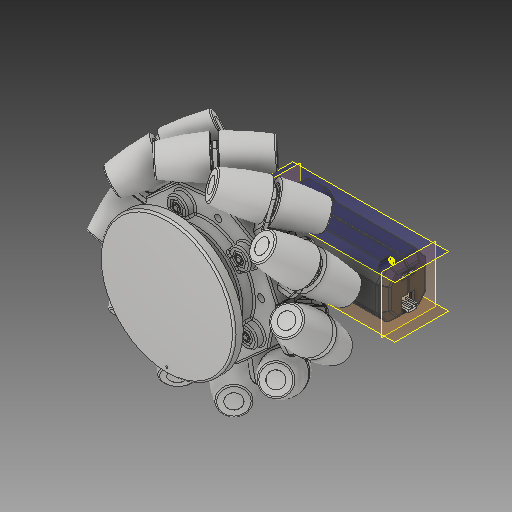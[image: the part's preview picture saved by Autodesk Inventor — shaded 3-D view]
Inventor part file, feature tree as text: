
AUTODESK INVENTOR PART (.ipt)
format: ipt  version: 2019 (Build 230136000, 136)  size: 17,352,704 bytes
history: native  units: in
note: dims shown in document units (in); Inventor stores cm internally (conversion verified against a paired STEP export)
features: other x108, plane x4
ambient origin geometry x8: Origin, YZ Plane, XZ Plane, XY Plane, X Axis, Y Axis, Z Axis, Center Point
bodies: Solid1 (feature_tree)
feature tree (112):
  other  "Wheel Sub-Assembly.iam"
  other  "wheel hubcap.ipt:1"
  other  "6inchMecanumLeft217-2799.20121203.iam:1::217-2799-001 Rev1.ipt:1"
  other  "6inchMecanumLeft217-2799.20121203.iam:1::217-2799-001 Rev1.ipt:2"
  other  "6inchMecanumLeft217-2799.20121203.iam:1::217-2799-002 Rev1.ipt:1"
  other  "6inchMecanumLeft217-2799.20121203.iam:1::217-2586-003 Rev2.ipt:1"
  other  "6inchMecanumLeft217-2799.20121203.iam:1::217-2586-003 Rev2.ipt:2"
  other  "6inchMecanumLeft217-2799.20121203.iam:1::217-2586-004 Rev1.ipt:1"
  other  "6inchMecanumLeft217-2799.20121203.iam:1::217-2586-004 Rev1.ipt:2"
  other  "6inchMecanumLeft217-2799.20121203.iam:1::217-2586-007 Rev1.ipt:1"
  other  "6inchMecanumLeft217-2799.20121203.iam:1::217-2586-008 Rev1.ipt:1"
  other  "6inchMecanumLeft217-2799.20121203.iam:1::NUT-832-NYLOCK.ipt:1"
  other  "6inchMecanumLeft217-2799.20121203.iam:1::SCREW-832-1250.ipt:1"
  other  "6inchMecanumLeft217-2799.20121203.iam:1::217-2586-007 Rev1.ipt:2"
  other  "6inchMecanumLeft217-2799.20121203.iam:1::217-2586-007 Rev1.ipt:3"
  other  "6inchMecanumLeft217-2799.20121203.iam:1::217-2586-007 Rev1.ipt:4"
  other  "6inchMecanumLeft217-2799.20121203.iam:1::217-2586-007 Rev1.ipt:5"
  other  "6inchMecanumLeft217-2799.20121203.iam:1::217-2586-007 Rev1.ipt:6"
  other  "6inchMecanumLeft217-2799.20121203.iam:1::217-2586-007 Rev1.ipt:7"
  other  "6inchMecanumLeft217-2799.20121203.iam:1::217-2586-007 Rev1.ipt:8"
  other  "6inchMecanumLeft217-2799.20121203.iam:1::217-2586-007 Rev1.ipt:9"
  other  "6inchMecanumLeft217-2799.20121203.iam:1::217-2586-007 Rev1.ipt:10"
  other  "6inchMecanumLeft217-2799.20121203.iam:1::217-2586-004 Rev1.ipt:3"
  other  "6inchMecanumLeft217-2799.20121203.iam:1::217-2586-004 Rev1.ipt:4"
  other  "6inchMecanumLeft217-2799.20121203.iam:1::217-2586-004 Rev1.ipt:5"
  other  "6inchMecanumLeft217-2799.20121203.iam:1::217-2586-004 Rev1.ipt:6"
  other  "6inchMecanumLeft217-2799.20121203.iam:1::217-2586-004 Rev1.ipt:7"
  other  "6inchMecanumLeft217-2799.20121203.iam:1::217-2586-004 Rev1.ipt:8"
  other  "6inchMecanumLeft217-2799.20121203.iam:1::217-2586-004 Rev1.ipt:9"
  other  "6inchMecanumLeft217-2799.20121203.iam:1::217-2586-004 Rev1.ipt:10"
  other  "6inchMecanumLeft217-2799.20121203.iam:1::217-2586-004 Rev1.ipt:11"
  other  "6inchMecanumLeft217-2799.20121203.iam:1::217-2586-004 Rev1.ipt:12"
  other  "6inchMecanumLeft217-2799.20121203.iam:1::217-2586-004 Rev1.ipt:13"
  other  "6inchMecanumLeft217-2799.20121203.iam:1::217-2586-004 Rev1.ipt:14"
  other  "6inchMecanumLeft217-2799.20121203.iam:1::217-2586-004 Rev1.ipt:15"
  other  "6inchMecanumLeft217-2799.20121203.iam:1::217-2586-004 Rev1.ipt:16"
  other  "6inchMecanumLeft217-2799.20121203.iam:1::217-2586-004 Rev1.ipt:17"
  other  "6inchMecanumLeft217-2799.20121203.iam:1::217-2586-004 Rev1.ipt:18"
  other  "6inchMecanumLeft217-2799.20121203.iam:1::217-2586-004 Rev1.ipt:19"
  other  "6inchMecanumLeft217-2799.20121203.iam:1::217-2586-004 Rev1.ipt:20"
  other  "6inchMecanumLeft217-2799.20121203.iam:1::217-2586-003 Rev2.ipt:3"
  other  "6inchMecanumLeft217-2799.20121203.iam:1::217-2586-003 Rev2.ipt:4"
  other  "6inchMecanumLeft217-2799.20121203.iam:1::217-2586-003 Rev2.ipt:5"
  other  "6inchMecanumLeft217-2799.20121203.iam:1::217-2586-003 Rev2.ipt:6"
  other  "6inchMecanumLeft217-2799.20121203.iam:1::217-2586-003 Rev2.ipt:7"
  other  "6inchMecanumLeft217-2799.20121203.iam:1::217-2586-003 Rev2.ipt:8"
  other  "6inchMecanumLeft217-2799.20121203.iam:1::217-2586-003 Rev2.ipt:9"
  other  "6inchMecanumLeft217-2799.20121203.iam:1::217-2586-003 Rev2.ipt:10"
  other  "6inchMecanumLeft217-2799.20121203.iam:1::217-2586-003 Rev2.ipt:11"
  other  "6inchMecanumLeft217-2799.20121203.iam:1::217-2586-003 Rev2.ipt:12"
  other  "6inchMecanumLeft217-2799.20121203.iam:1::217-2586-003 Rev2.ipt:13"
  other  "6inchMecanumLeft217-2799.20121203.iam:1::217-2586-003 Rev2.ipt:14"
  other  "6inchMecanumLeft217-2799.20121203.iam:1::217-2586-003 Rev2.ipt:15"
  other  "6inchMecanumLeft217-2799.20121203.iam:1::217-2586-003 Rev2.ipt:16"
  other  "6inchMecanumLeft217-2799.20121203.iam:1::217-2586-003 Rev2.ipt:17"
  other  "6inchMecanumLeft217-2799.20121203.iam:1::217-2586-003 Rev2.ipt:18"
  other  "6inchMecanumLeft217-2799.20121203.iam:1::217-2586-003 Rev2.ipt:19"
  other  "6inchMecanumLeft217-2799.20121203.iam:1::217-2586-003 Rev2.ipt:20"
  other  "6inchMecanumLeft217-2799.20121203.iam:1::217-2799-002 Rev1.ipt:2"
  other  "6inchMecanumLeft217-2799.20121203.iam:1::217-2799-002 Rev1.ipt:3"
  other  "6inchMecanumLeft217-2799.20121203.iam:1::217-2799-002 Rev1.ipt:4"
  other  "6inchMecanumLeft217-2799.20121203.iam:1::217-2799-002 Rev1.ipt:5"
  other  "6inchMecanumLeft217-2799.20121203.iam:1::217-2799-002 Rev1.ipt:6"
  other  "6inchMecanumLeft217-2799.20121203.iam:1::217-2799-002 Rev1.ipt:7"
  other  "6inchMecanumLeft217-2799.20121203.iam:1::217-2799-002 Rev1.ipt:8"
  other  "6inchMecanumLeft217-2799.20121203.iam:1::217-2799-002 Rev1.ipt:9"
  other  "6inchMecanumLeft217-2799.20121203.iam:1::217-2799-002 Rev1.ipt:10"
  other  "6inchMecanumLeft217-2799.20121203.iam:1::217-2586-008 Rev1.ipt:2"
  other  "6inchMecanumLeft217-2799.20121203.iam:1::217-2586-008 Rev1.ipt:3"
  other  "6inchMecanumLeft217-2799.20121203.iam:1::217-2586-008 Rev1.ipt:4"
  other  "6inchMecanumLeft217-2799.20121203.iam:1::217-2586-008 Rev1.ipt:5"
  other  "6inchMecanumLeft217-2799.20121203.iam:1::217-2586-008 Rev1.ipt:6"
  other  "6inchMecanumLeft217-2799.20121203.iam:1::SCREW-832-1250.ipt:2"
  other  "6inchMecanumLeft217-2799.20121203.iam:1::SCREW-832-1250.ipt:3"
  other  "6inchMecanumLeft217-2799.20121203.iam:1::SCREW-832-1250.ipt:4"
  other  "6inchMecanumLeft217-2799.20121203.iam:1::SCREW-832-1250.ipt:5"
  other  "6inchMecanumLeft217-2799.20121203.iam:1::NUT-832-NYLOCK.ipt:2"
  other  "6inchMecanumLeft217-2799.20121203.iam:1::NUT-832-NYLOCK.ipt:3"
  other  "6inchMecanumLeft217-2799.20121203.iam:1::NUT-832-NYLOCK.ipt:4"
  other  "6inchMecanumLeft217-2799.20121203.iam:1::NUT-832-NYLOCK.ipt:5"
  other  "6inchMecanumLeft217-2799.20121203.iam:1::217-2586-005 Rev2.ipt:1"
  other  "6inchMecanumLeft217-2799.20121203.iam:1::217-2586-005 Rev2.ipt:2"
  other  "6inchMecanumLeft217-2799.20121203.iam:1::217-2586-005 Rev2.ipt:3"
  other  "6inchMecanumLeft217-2799.20121203.iam:1::217-2586-005 Rev2.ipt:4"
  other  "6inchMecanumLeft217-2799.20121203.iam:1::217-2586-005 Rev2.ipt:5"
  other  "6inchMecanumLeft217-2799.20121203.iam:1::217-2586-005 Rev2.ipt:6"
  other  "6inchMecanumLeft217-2799.20121203.iam:1::217-2586-005 Rev2.ipt:7"
  other  "6inchMecanumLeft217-2799.20121203.iam:1::217-2586-005 Rev2.ipt:8"
  other  "6inchMecanumLeft217-2799.20121203.iam:1::217-2586-005 Rev2.ipt:9"
  other  "6inchMecanumLeft217-2799.20121203.iam:1::217-2586-005 Rev2.ipt:10"
  other  "6inchMecanumLeft217-2799.20121203.iam:1::217-2586-005 Rev2.ipt:11"
  other  "6inchMecanumLeft217-2799.20121203.iam:1::217-2586-005 Rev2.ipt:12"
  other  "6inchMecanumLeft217-2799.20121203.iam:1::217-2586-005 Rev2.ipt:13"
  other  "6inchMecanumLeft217-2799.20121203.iam:1::217-2586-005 Rev2.ipt:14"
  other  "6inchMecanumLeft217-2799.20121203.iam:1::217-2586-005 Rev2.ipt:15"
  other  "6inchMecanumLeft217-2799.20121203.iam:1::217-2586-005 Rev2.ipt:16"
  other  "6inchMecanumLeft217-2799.20121203.iam:1::217-2586-005 Rev2.ipt:17"
  other  "6inchMecanumLeft217-2799.20121203.iam:1::217-2586-005 Rev2.ipt:18"
  other  "6inchMecanumLeft217-2799.20121203.iam:1::217-2586-005 Rev2.ipt:19"
  other  "6inchMecanumLeft217-2799.20121203.iam:1::217-2586-005 Rev2.ipt:20"
  other  "REV-41-1300HexMotor.ipt:1"
  other  "REV-41-1349HexAxle.ipt:1"
  other  "VersaHub 500 Hex.ipt:1"
  other  "545690 assembly.ipt:1"
  other  "Wheel Sub-Assembly.iam_Bodies"
  plane  "Work Plane1"
  plane  "Work Plane2"
  plane  "Work Plane3"
  plane  "Work Plane4"
  other  "Srf1"
  other  "Work Axis1"
  other  "Srf1::Derived"
